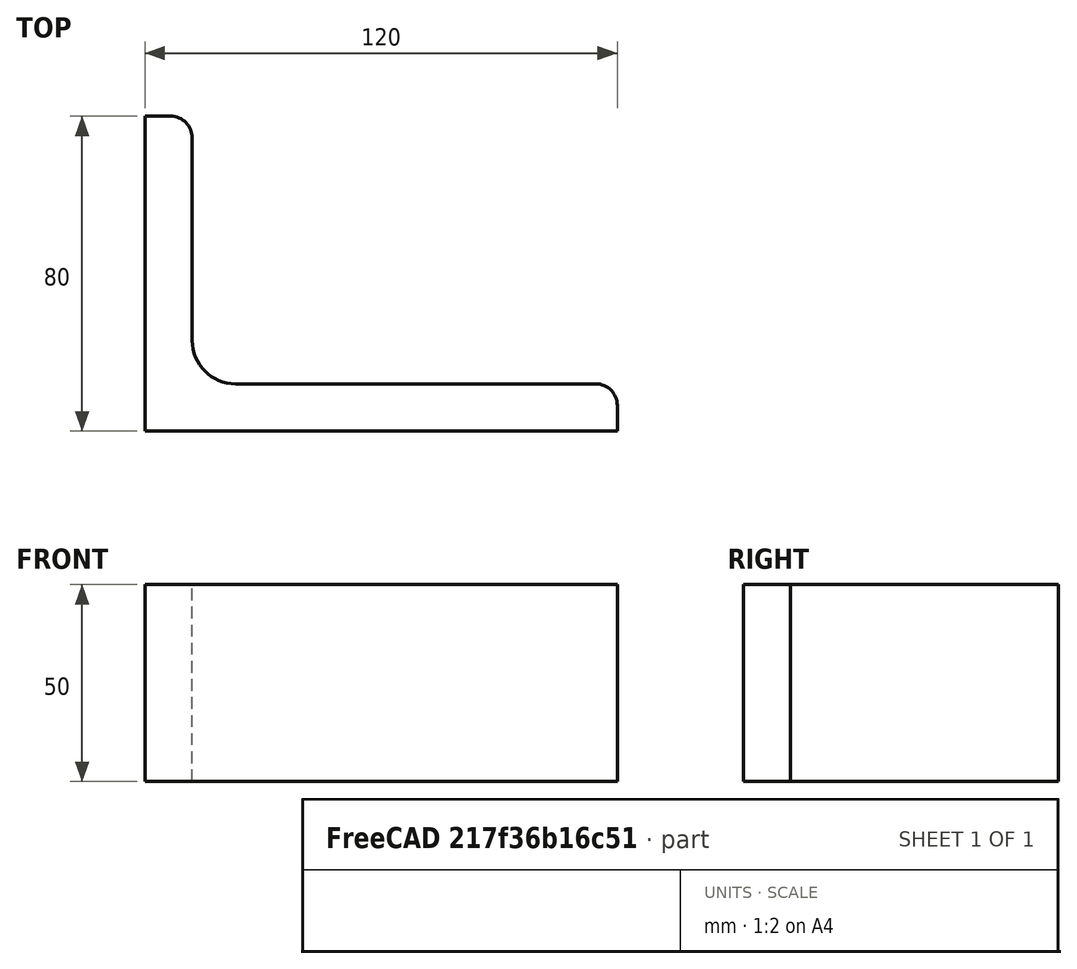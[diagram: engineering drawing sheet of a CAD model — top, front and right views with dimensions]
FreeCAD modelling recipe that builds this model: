
FCSTD DOCUMENT  (FreeCAD 0.15R4671 (Git))
Label: Angle Bar 120x80x12 EN10056 S235JR
License: All rights reserved
LicenseURL: http://en.wikipedia.org/wiki/All_rights_reserved
objects: Sketcher::SketchObject×1, Part::Extrusion×1
note: 2 computed .brp shape members not serialized (recipe doc carries the construction recipe); baked Part::Feature solids carry a one-line shape summary decoded from their .brp

FEATURE [Sketcher::SketchObject] Sketch
  sketch-geometry (9):
    g0: LineSegment StartX=0 StartY=0 StartZ=0 EndX=120 EndY=0 EndZ=0
    g1: LineSegment StartX=120 StartY=0 StartZ=0 EndX=120 EndY=6.5 EndZ=0
    g2: LineSegment StartX=114.5 StartY=12 StartZ=0 EndX=23 EndY=12 EndZ=0
    g3: LineSegment StartX=0 StartY=0 StartZ=0 EndX=0 EndY=80 EndZ=0
    g4: LineSegment StartX=0 StartY=80 StartZ=0 EndX=6.5 EndY=80 EndZ=0
    g5: LineSegment StartX=12 StartY=74.5 StartZ=0 EndX=12 EndY=23 EndZ=0
    g6: ArcOfCircle CenterX=23 CenterY=23 CenterZ=0 NormalX=0 NormalY=0 NormalZ=1 Radius=11 StartAngle=3.14159 EndAngle=4.71239
    g7: ArcOfCircle CenterX=6.5 CenterY=74.5 CenterZ=0 NormalX=0 NormalY=0 NormalZ=1 Radius=5.5 StartAngle=0 EndAngle=1.5708
    g8: ArcOfCircle CenterX=114.5 CenterY=6.5 CenterZ=0 NormalX=0 NormalY=0 NormalZ=1 Radius=5.5 StartAngle=0 EndAngle=1.5708
  constraints (23):
    c: Coincident(g0,g-1)
    c: Horizontal(g0)
    c: Coincident(g1,g0)
    c: Vertical(g1)
    c: Horizontal(g2)
    c: Coincident(g3,g-1)
    c: Vertical(g3)
    c: Coincident(g4,g3)
    c: Horizontal(g4)
    c: Vertical(g5)
    c: Tangent(g5,g6) = -1.5708
    c: Tangent(g2,g6) = 1.5708
    c: Tangent(g4,g7) = 1.5708
    c: Tangent(g5,g7) = 1.5708
    c: Tangent(g2,g8) = -1.5708
    c: Tangent(g1,g8) = -1.5708
    c: DistanceX(g0) = 120
    c: DistanceY(g3) = 80
    c: DistanceY(g0,g2) = 12
    c: DistanceX(g3,g5) = 12
    c: Radius(g6) = 11
    c: Radius(g8) = 5.5
    c: Radius(g7) = 5.5
FEATURE [Part::Extrusion] Extrude  label="Angle Bar 120x80x12 EN10056 S235JR"
  Base = -> Sketch
  Dir = (0,0,50)
  Solid = true
